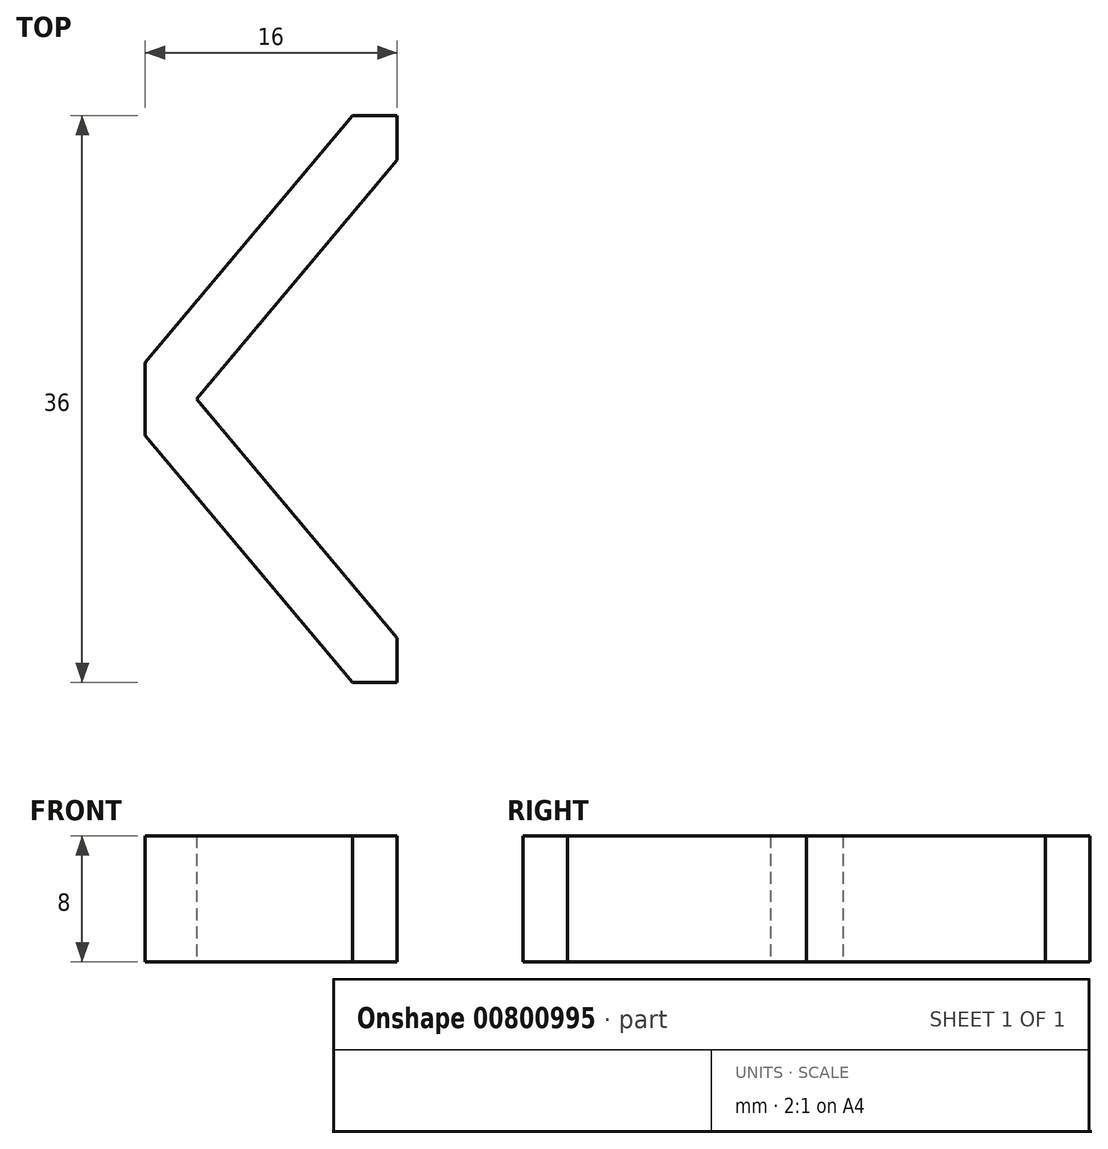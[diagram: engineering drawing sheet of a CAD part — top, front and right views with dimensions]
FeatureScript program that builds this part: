
annotation { "Feature Type Name" : "Feature", "Feature Type Description" : "" }
export const myFeature = defineFeature(function(context is Context, id is Id, definition is map)
    precondition{}
    {
        {
            var Q0;
            Q0=qCreatedBy(makeId("Top.planeOp"),FACE);
            var sketch = newSketch(context, id + "F0", { "sketchPlane" : qUnion([Q0])});
            skLineSegment(sketch, "E0", {"start": v(13.17, 0) * mm, "end": v(0, -15.7) * mm});
            skLineSegment(sketch, "E1", {"start": v(0, -15.7) * mm, "end": v(0, -20.3) * mm});
            skLineSegment(sketch, "E2", {"start": v(0, -20.3) * mm, "end": v(13.17, -36) * mm});
            skLineSegment(sketch, "E3", {"start": v(13.17, -36) * mm, "end": v(16, -36) * mm});
            skLineSegment(sketch, "E4", {"start": v(16, -36) * mm, "end": v(16, -33.17) * mm});
            skLineSegment(sketch, "E5", {"start": v(16, -33.17) * mm, "end": v(3.27, -18) * mm});
            skLineSegment(sketch, "E6", {"start": v(3.27, -18) * mm, "end": v(16, -2.83) * mm});
            skLineSegment(sketch, "E7", {"start": v(16, -2.83) * mm, "end": v(16, 0) * mm});
            skLineSegment(sketch, "E8", {"start": v(16, 0) * mm, "end": v(13.17, 0) * mm});
            skSolve(sketch);
        }
        {
            var Q0;
            Q0=makeQuery(id+"F0.imprint","IMPRINT",FACE,{"disambiguationData":[TD([[makeQuery(id+"F0.imprint","IMPRINT",EDGE,{"derivedFrom":sQuery(id+"F0.wireOp",EDGE,"E0")}),1.0]])]});
            extrude(context, id + "F1", {"entities" : qUnion([Q0]), "depth" : 8 * mm, "offsetDistance" : 25 * mm});
        }
    });
